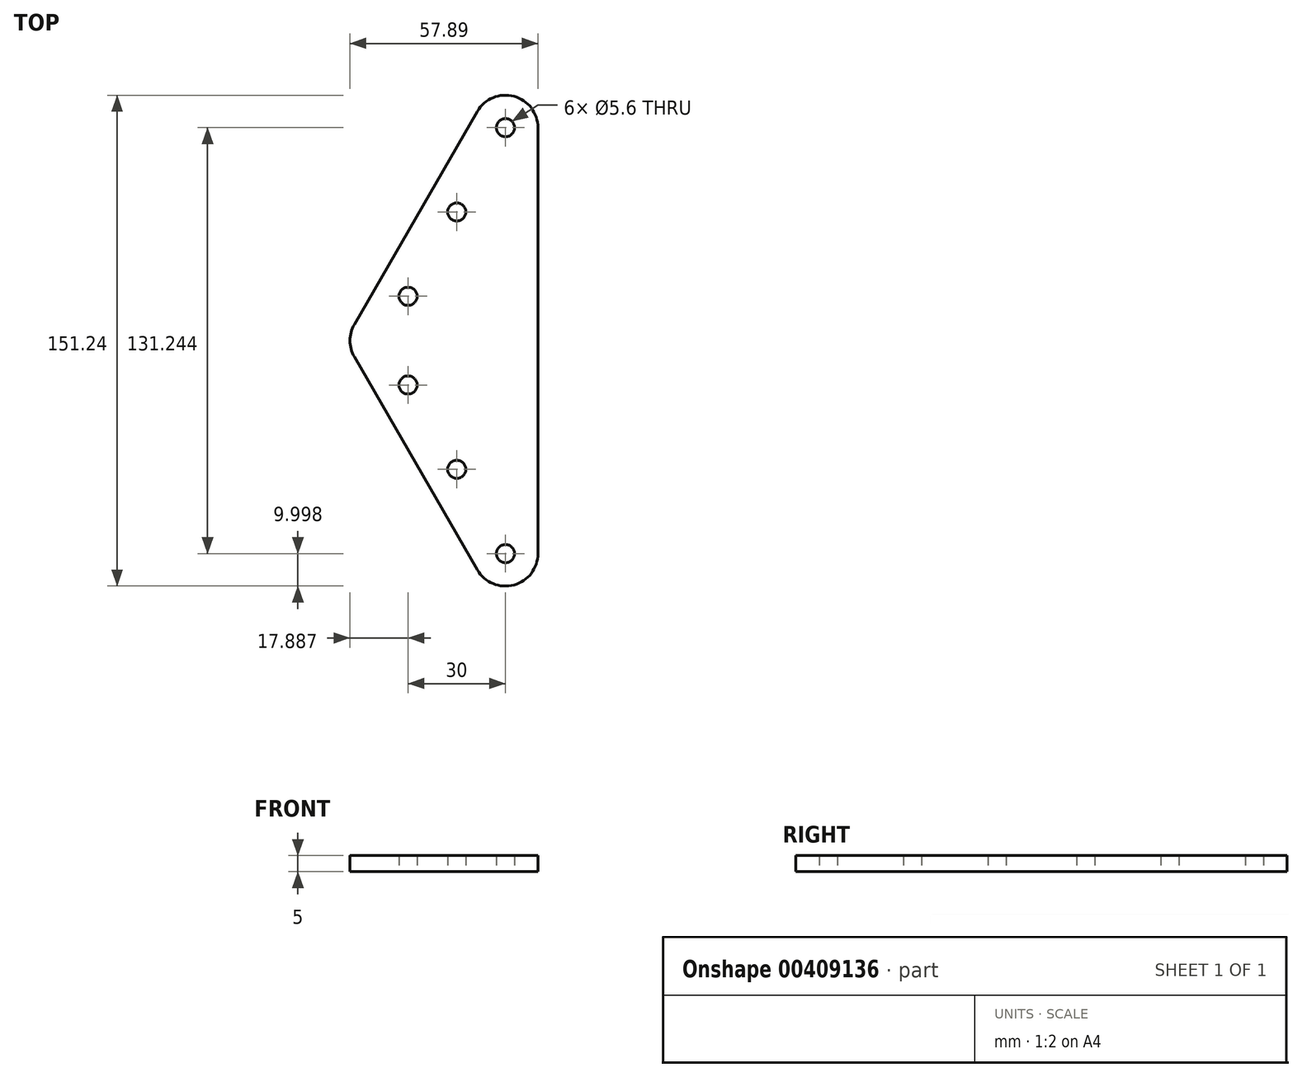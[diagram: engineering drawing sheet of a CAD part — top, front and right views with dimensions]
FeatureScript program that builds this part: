
annotation { "Feature Type Name" : "Feature", "Feature Type Description" : "" }
export const myFeature = defineFeature(function(context is Context, id is Id, definition is map)
    precondition{}
    {
        {
            var Q0;
            Q0=qCreatedBy(makeId("Top.planeOp"), FACE);
            var sketch = newSketch(context, id + "F0", { "sketchPlane" : qUnion([Q0])});
            skLineSegment(sketch, "E0", {"start": v(0, 0) * mm, "end": v(47.89, 0) * mm, "construction": true});
            skLineSegment(sketch, "E1", {"start": v(47.89, 0) * mm, "end": v(47.89, 65.62) * mm});
            skLineSegment(sketch, "E2", {"start": v(47.89, 82.94) * mm, "end": v(0, 0) * mm, "construction": true});
            skLineSegment(sketch, "E3", {"start": v(47.89, 102.94) * mm, "end": v(29.23, 70.62) * mm, "construction": true});
            skLineSegment(sketch, "E4", {"start": v(47.89, 62.94) * mm, "end": v(37.89, 45.62) * mm, "construction": true});
            skLineSegment(sketch, "E5", {"start": v(-5.77, 10) * mm, "end": v(11.55, 0) * mm, "construction": true});
            skCircle(sketch, "E6", {"center": v(7.89, 13.66) * mm, "radius": 2.8 * mm});
            skCircle(sketch, "E7", {"center": v(22.89, 39.64) * mm, "radius": 2.8 * mm});
            skCircle(sketch, "E8", {"center": v(37.89, 65.62) * mm, "radius": 2.8 * mm});
            skCircle(sketch, "E9", {"center": v(22.89, 39.64) * mm, "radius": 30 * mm, "construction": true});
            skCircle(sketch, "E10", {"center": v(7.89, 13.66) * mm, "radius": 10 * mm, "construction": true});
            skLineSegment(sketch, "E11", {"start": v(47.89, 75.62) * mm, "end": v(37.89, 75.62) * mm, "construction": true});
            skLineSegment(sketch, "E12", {"start": v(29.23, 70.62) * mm, "end": v(-8.66, 5) * mm});
            skLineSegment(sketch, "E13", {"start": v(47.89, 65.62) * mm, "end": v(47.89, 102.94) * mm, "construction": true});
            skLineSegment(sketch, "E14", {"start": v(0, 0) * mm, "end": v(-10, 0) * mm, "construction": true});
            skArc(sketch, "E15", {"start": v(29.23, 70.62) * mm, "mid": v(35.3, 55.96) * mm, "end": v(47.89, 65.62) * mm, "construction": true});
            skArc(sketch, "E16", {"start": v(47.89, 65.62) * mm, "mid": v(40.47, 75.28) * mm, "end": v(29.23, 70.62) * mm});
            skArc(sketch, "E17", {"start": v(-8.66, 5) * mm, "mid": v(-9.66, 2.59) * mm, "end": v(-10, 0) * mm});
            skArc(sketch, "E18", {"start": v(-10, 0) * mm, "mid": v(9.66, -2.59) * mm, "end": v(-8.66, 5) * mm, "construction": true});
            skLineSegment(sketch, "E19", {"start": v(13, 2.5) * mm, "end": v(37.89, 2.5) * mm, "construction": true});
            skLineSegment(sketch, "E20", {"start": v(37.89, 2.5) * mm, "end": v(37.89, 45.62) * mm, "construction": true});
            skLineSegment(sketch, "E21", {"start": v(37.89, 45.62) * mm, "end": v(13, 2.5) * mm, "construction": true});
            skLineSegment(sketch, "E22", {"start": v(13, 2.5) * mm, "end": v(8.66, -5) * mm, "construction": true});
            skLineSegment(sketch, "E23.MirrorCS", {"start": v(47.89, -75.62) * mm, "end": v(37.89, -75.62) * mm, "construction": true});
            skLineSegment(sketch, "E24.MirrorCS", {"start": v(47.89, -62.94) * mm, "end": v(37.89, -45.62) * mm, "construction": true});
            skLineSegment(sketch, "E25.MirrorCS", {"start": v(37.89, -45.62) * mm, "end": v(13, -2.5) * mm, "construction": true});
            skLineSegment(sketch, "E26.MirrorCS", {"start": v(29.23, -70.62) * mm, "end": v(-8.66, -5) * mm});
            skArc(sketch, "E27.MirrorCS", {"start": v(-8.66, -5) * mm, "mid": v(-9.66, -2.59) * mm, "end": v(-10, 0) * mm});
            skCircle(sketch, "E28.MirrorC", {"center": v(22.89, -39.64) * mm, "radius": 30 * mm, "construction": true});
            skArc(sketch, "E29.MirrorCS", {"start": v(-10, 0) * mm, "mid": v(9.66, 2.59) * mm, "end": v(-8.66, -5) * mm, "construction": true});
            skLineSegment(sketch, "E30.MirrorCS", {"start": v(37.89, -2.5) * mm, "end": v(37.89, -45.62) * mm, "construction": true});
            skArc(sketch, "E31.MirrorCS", {"start": v(29.23, -70.62) * mm, "mid": v(35.3, -55.96) * mm, "end": v(47.89, -65.62) * mm, "construction": true});
            skLineSegment(sketch, "E32.MirrorCS", {"start": v(13, -2.5) * mm, "end": v(8.66, 5) * mm, "construction": true});
            skCircle(sketch, "E33.MirrorC", {"center": v(7.89, -13.66) * mm, "radius": 2.8 * mm});
            skLineSegment(sketch, "E34.MirrorCS", {"start": v(47.89, 0) * mm, "end": v(47.89, -65.62) * mm});
            skLineSegment(sketch, "E35.MirrorCS", {"start": v(-5.77, -10) * mm, "end": v(11.55, 0) * mm, "construction": true});
            skArc(sketch, "E36.MirrorCS", {"start": v(47.89, -65.62) * mm, "mid": v(40.47, -75.28) * mm, "end": v(29.23, -70.62) * mm});
            skCircle(sketch, "E37.MirrorC", {"center": v(22.89, -39.64) * mm, "radius": 2.8 * mm});
            skCircle(sketch, "E38.MirrorC", {"center": v(7.89, -13.66) * mm, "radius": 10 * mm, "construction": true});
            skLineSegment(sketch, "E39.MirrorCS", {"start": v(47.89, -82.94) * mm, "end": v(0, 0) * mm, "construction": true});
            skLineSegment(sketch, "E40.MirrorCS", {"start": v(13, -2.5) * mm, "end": v(37.89, -2.5) * mm, "construction": true});
            skCircle(sketch, "E41.MirrorC", {"center": v(37.89, -65.62) * mm, "radius": 2.8 * mm});
            skSolve(sketch);
        }
        {
            var Q0;
            Q0 = qSketchRegion(id + "F0", true);
            extrude(context, id + "F1", {"entities" : qUnion([Q0]), "depth" : 5 * mm, "offsetDistance" : 25 * mm});
        }
    });
